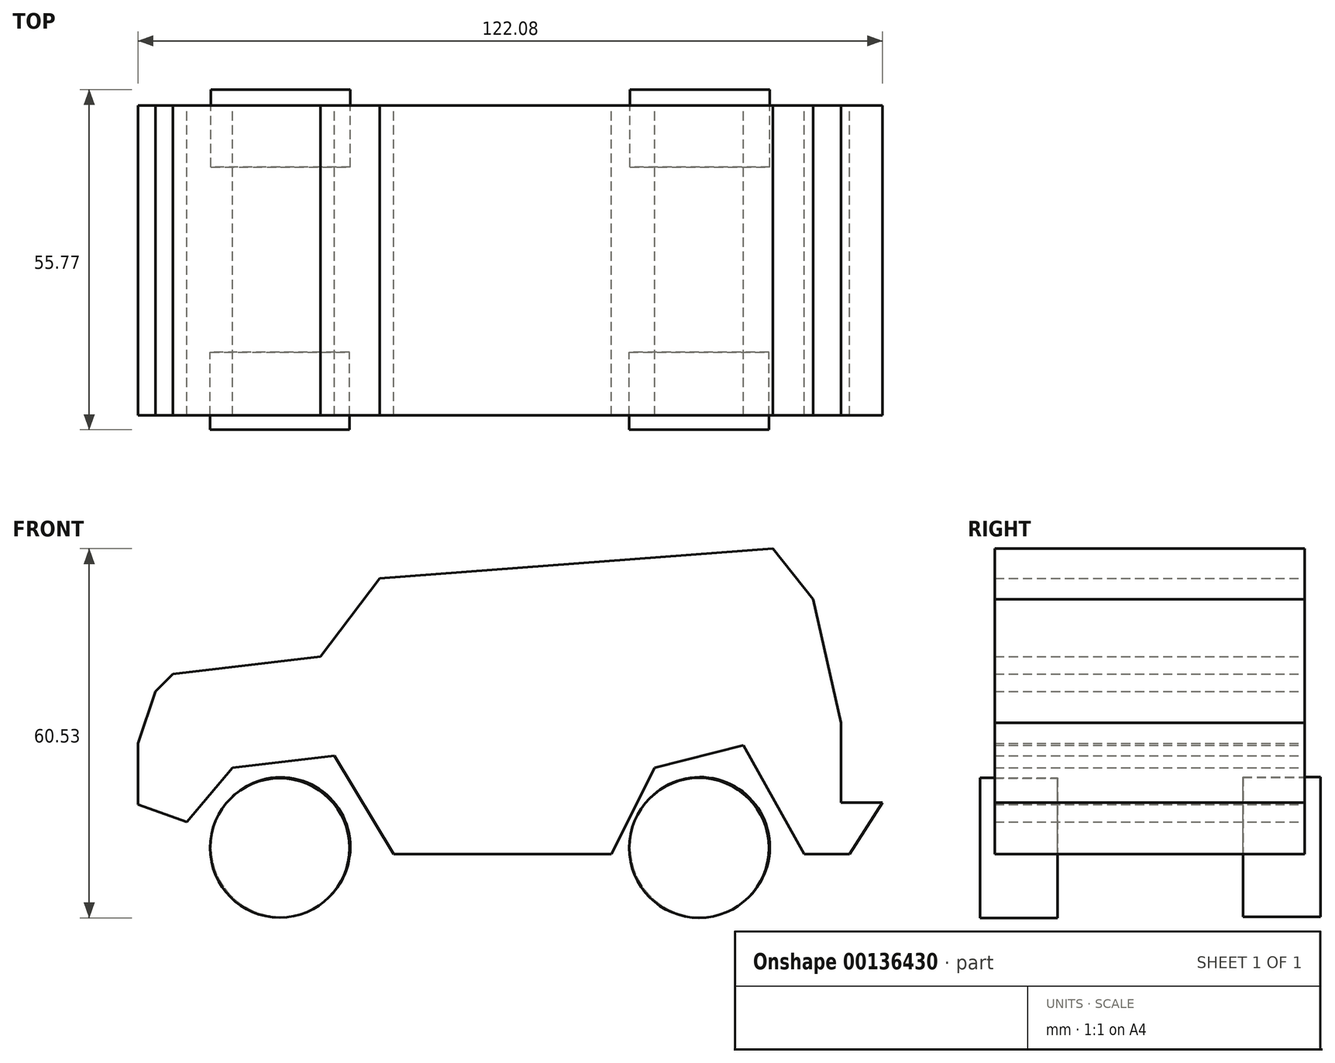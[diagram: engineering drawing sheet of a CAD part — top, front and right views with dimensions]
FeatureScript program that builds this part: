
annotation { "Feature Type Name" : "Feature", "Feature Type Description" : "" }
export const myFeature = defineFeature(function(context is Context, id is Id, definition is map)
    precondition{}
    {
        {
            var Q0;
            Q0=qCreatedBy(makeId("Front.planeOp"),FACE);
            var sketch = newSketch(context, id + "F0", { "sketchPlane" : qUnion([Q0])});
            skLineSegment(sketch, "E0", {"start": v(-56.2, 8.13) * mm, "end": v(-48.2, 5.28) * mm});
            skLineSegment(sketch, "E1", {"start": v(-56.2, 8.13) * mm, "end": v(-56.2, 18.11) * mm});
            skLineSegment(sketch, "E2", {"start": v(-56.2, 18.11) * mm, "end": v(-53.34, 26.67) * mm});
            skLineSegment(sketch, "E3", {"start": v(-53.34, 26.67) * mm, "end": v(-50.49, 29.52) * mm});
            skLineSegment(sketch, "E4", {"start": v(-50.49, 29.52) * mm, "end": v(-26.24, 32.37) * mm});
            skLineSegment(sketch, "E5", {"start": v(-26.24, 32.37) * mm, "end": v(-16.54, 45.21) * mm});
            skLineSegment(sketch, "E6", {"start": v(-16.54, 45.21) * mm, "end": v(47.92, 50.06) * mm});
            skLineSegment(sketch, "E7", {"start": v(47.92, 50.06) * mm, "end": v(54.48, 41.79) * mm});
            skLineSegment(sketch, "E8", {"start": v(54.48, 41.79) * mm, "end": v(59.04, 21.54) * mm});
            skLineSegment(sketch, "E9", {"start": v(59.04, 21.54) * mm, "end": v(59.04, 8.41) * mm});
            skLineSegment(sketch, "E10", {"start": v(59.04, 8.41) * mm, "end": v(65.9, 8.41) * mm});
            skLineSegment(sketch, "E11", {"start": v(65.9, 8.41) * mm, "end": v(60.47, 0) * mm});
            skLineSegment(sketch, "E12", {"start": v(60.47, 0) * mm, "end": v(53.05, 0) * mm});
            skLineSegment(sketch, "E13", {"start": v(53.05, 0) * mm, "end": v(43.07, 17.83) * mm});
            skLineSegment(sketch, "E14", {"start": v(43.07, 17.83) * mm, "end": v(28.52, 14.12) * mm});
            skLineSegment(sketch, "E15", {"start": v(28.52, 14.12) * mm, "end": v(21.4, 0) * mm});
            skLineSegment(sketch, "E16", {"start": v(21.4, 0) * mm, "end": v(-14.26, 0) * mm});
            skLineSegment(sketch, "E17", {"start": v(-14.26, 0) * mm, "end": v(-23.96, 16.12) * mm});
            skLineSegment(sketch, "E18", {"start": v(-23.96, 16.12) * mm, "end": v(-40.68, 14.15) * mm});
            skLineSegment(sketch, "E19", {"start": v(-40.68, 14.15) * mm, "end": v(-48.2, 5.28) * mm});
            skSolve(sketch);
        }
        {
            var Q0;
            Q0=makeQuery(id+"F0.imprint","IMPRINT",FACE,{"disambiguationData":[TD([[makeQuery(id+"F0.imprint","IMPRINT",EDGE,{"derivedFrom":sQuery(id+"F0.wireOp",EDGE,"E0")}),1.0]])]});
            extrude(context, id + "F1", {"entities" : qUnion([Q0]), "depth" : 50.8 * mm});
        }
        {
            var Q0;
            Q0=qCreatedBy(makeId("Front.planeOp"),FACE);
            var sketch = newSketch(context, id + "F2", { "sketchPlane" : qUnion([Q0])});
            skCircle(sketch, "E20", {"center": v(-32.8, 0) * mm, "radius": 11.43 * mm});
            skCircle(sketch, "E21", {"center": v(35.94, 0) * mm, "radius": 11.47 * mm});
            skCircle(sketch, "E22", {"center": v(-51.77, -37.5) * mm, "radius": 11.43 * mm});
            skCircle(sketch, "E23", {"center": v(16.97, -37.5) * mm, "radius": 11.47 * mm});
            skSolve(sketch);
        }
        {
            var Q0;
            Q0 = qSketchRegion(id + "F2", true);
            extrude(context, id + "F3", {"entities" : qUnion([Q0]), "depth" : 12.7 * mm});
        }
        {
            var Q0;
            Q0=makeQuery(id+"F3.opExtrude","SWEPT_BODY",BODY,{"disambiguationData":[OSD([sQuery(id+"F2.wireOp",EDGE,"E22")])]});
            var Q1;
            Q1=makeQuery(id+"F3.opExtrude","SWEPT_BODY",BODY,{"disambiguationData":[OSD([sQuery(id+"F2.wireOp",EDGE,"E23")])]});
            transform(context, id + "F4", {"entities" : qUnion([Q0, Q1]), "transformType" : TransformType.TRANSLATION_3D, "dx" : 18.83 * mm, "dy" : -40.5 * mm, "dz" : 38.5 * mm, "makeCopy" : false});
        }
        {
            var Q0;
            Q0=makeQuery(id+"F3.opExtrude","SWEPT_BODY",BODY,{"disambiguationData":[OSD([sQuery(id+"F2.wireOp",EDGE,"E21")])]});
            var Q1;
            Q1=makeQuery(id+"F3.opExtrude","SWEPT_BODY",BODY,{"disambiguationData":[OSD([sQuery(id+"F2.wireOp",EDGE,"E20")])]});
            transform(context, id + "F5", {"entities" : qUnion([Q0, Q1]), "transformType" : TransformType.TRANSLATION_3D, "dx" : 0 * mm, "dy" : 2.57 * mm, "dz" : 1.14 * mm, "makeCopy" : false});
        }
    });
